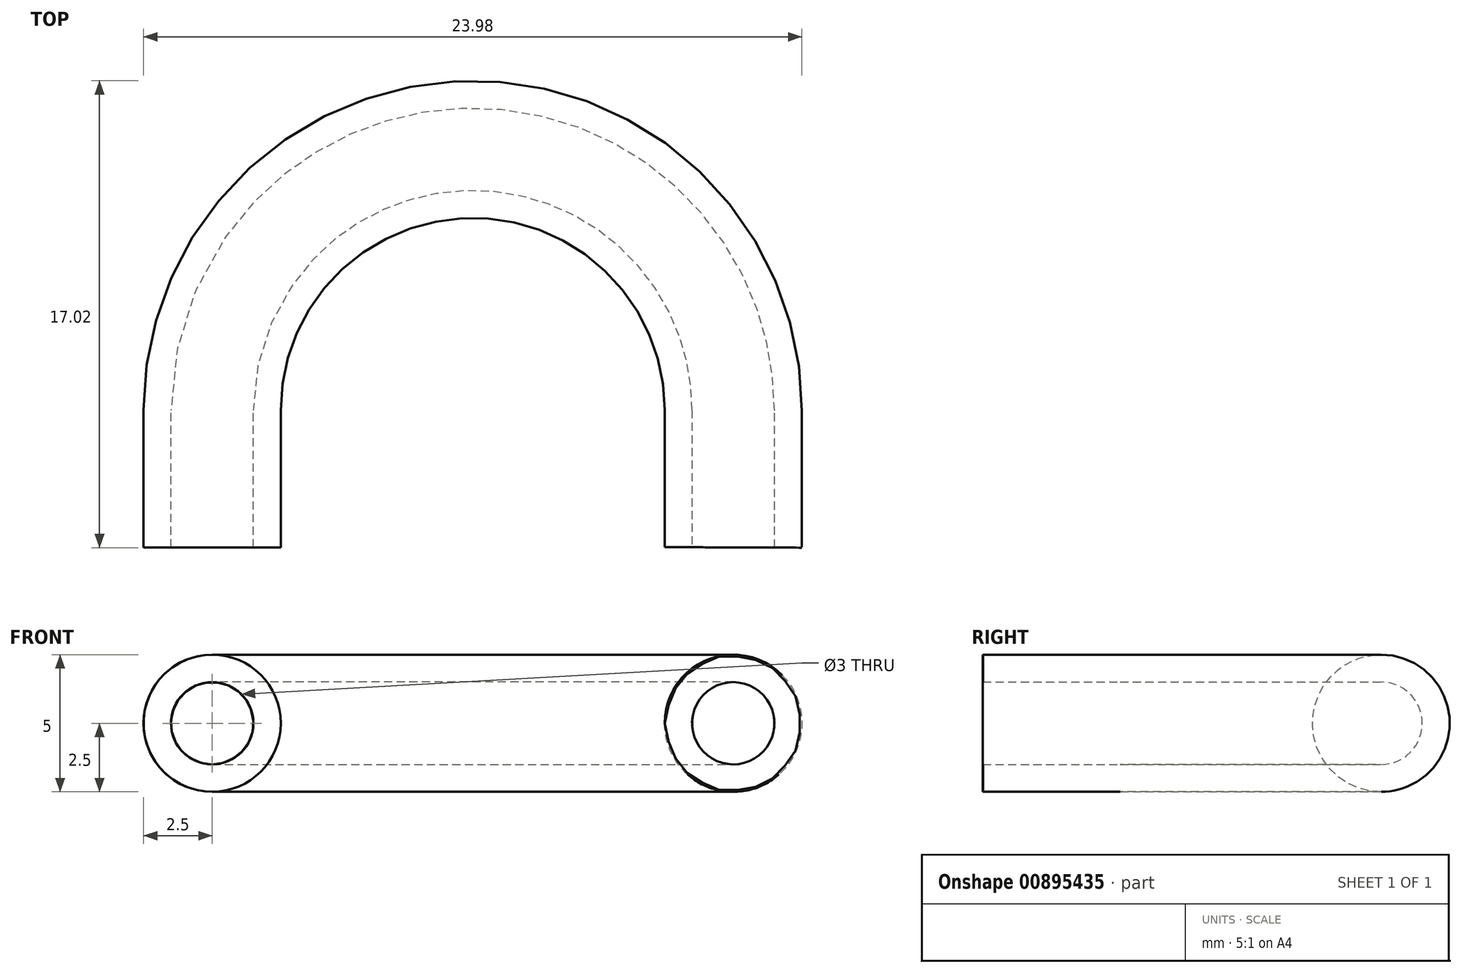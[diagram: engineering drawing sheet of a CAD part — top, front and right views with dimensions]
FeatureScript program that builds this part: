
annotation { "Feature Type Name" : "Feature", "Feature Type Description" : "" }
export const myFeature = defineFeature(function(context is Context, id is Id, definition is map)
    precondition{}
    {
        {
            var Q0;
            Q0=qCreatedBy(makeId("Top.planeOp"),FACE);
            var sketch = newSketch(context, id + "F0", { "sketchPlane" : qUnion([Q0])});
            skArc(sketch, "E0", {"start": v(18.98, 0) * mm, "mid": v(9.49, 9.5) * mm, "end": v(0, 0) * mm});
            skSolve(sketch);
        }
        {
            var Q0;
            Q0=qCreatedBy(makeId("Front.planeOp"),FACE);
            var sketch = newSketch(context, id + "F1", { "sketchPlane" : qUnion([Q0])});
            skCircle(sketch, "E1", {"center": v(0, 0) * mm, "radius": 2.5 * mm});
            skSolve(sketch);
        }
        {
            var Q0;
            Q0=makeQuery(id+"F1.imprint","IMPRINT",FACE,{"disambiguationData":[TD([[makeQuery(id+"F1.imprint","IMPRINT",EDGE,{"derivedFrom":sQuery(id+"F1.wireOp",EDGE,"E1")}),1.0]])]});
            var Q1;
            Q1=sQuery(id+"F0.wireOp",EDGE,"E0");
            sweep(context, id + "F2", {"profiles" : qUnion([Q0]), "path" : qUnion([Q1])});
        }
        {
            var Q0;
            Q0=makeQuery(id+"F2.opSweep","CAP_FACE",FACE,{"disambiguationData":[OSD([sQuery(id+"F0.wireOp",VERTEX,"E0.end"),sQuery(id+"F1.wireOp",EDGE,"E1")])],"isStart":true});
            var Q1;
            Q1=makeQuery(id+"F2.opSweep","CAP_FACE",FACE,{"disambiguationData":[OSD([sQuery(id+"F0.wireOp",VERTEX,"E0.start"),sQuery(id+"F1.wireOp",EDGE,"E1")])],"isStart":false});
            extrude(context, id + "F3", {"entities" : qUnion([Q0, Q1]), "operationType" : NewBodyOperationType.ADD, "depth" : 5 * mm, "offsetDistance" : 25 * mm});
        }
        {
            var Q0;
            Q0=makeQuery(id+"F3.opExtrude","CAP_FACE",FACE,{"disambiguationData":[OSD([sQuery(id+"F0.wireOp",VERTEX,"E0.start"),sQuery(id+"F1.wireOp",EDGE,"E1")]),OD(0.0)],"isStart":false});
            var Q1;
            Q1=makeQuery(id+"F3.opExtrude","CAP_FACE",FACE,{"disambiguationData":[OSD([sQuery(id+"F0.wireOp",VERTEX,"E0.end"),sQuery(id+"F1.wireOp",EDGE,"E1")])],"isStart":false});
            shell(context, id + "F4", {"entities" : qUnion([Q0, Q1]), "thickness" : 1 * mm});
        }
    });
